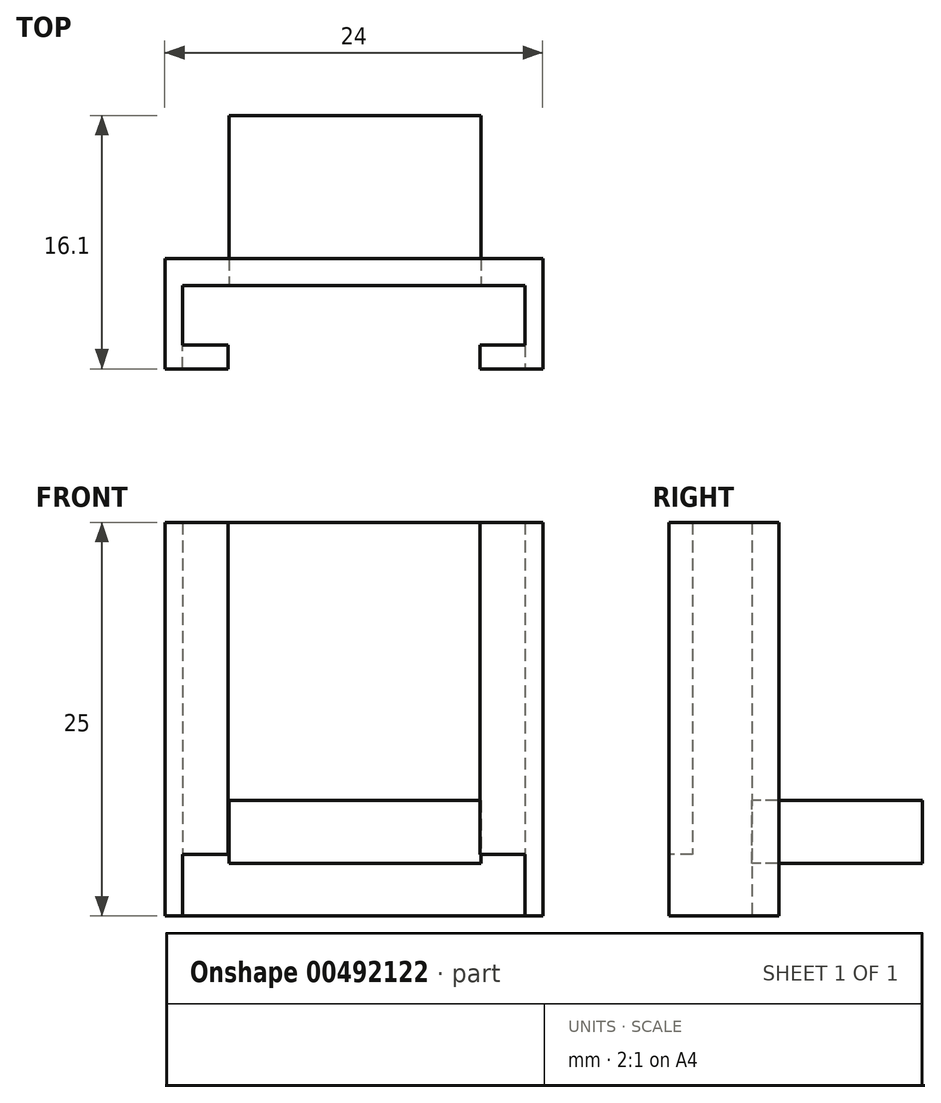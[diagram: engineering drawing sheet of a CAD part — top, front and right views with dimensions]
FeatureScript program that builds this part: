
annotation { "Feature Type Name" : "Feature", "Feature Type Description" : "" }
export const myFeature = defineFeature(function(context is Context, id is Id, definition is map)
    precondition{}
    {
        {
            var Q0;
            Q0=qCreatedBy(makeId("Top.planeOp"),FACE);
            var sketch = newSketch(context, id + "F0", { "sketchPlane" : qUnion([Q0])});
            skLineSegment(sketch, "E0", {"start": v(-20.1, 8.38) * mm, "end": v(-8.1, 8.38) * mm});
            skLineSegment(sketch, "E1", {"start": v(-8.1, 8.38) * mm, "end": v(-8.1, 1.38) * mm});
            skLineSegment(sketch, "E2", {"start": v(-8.1, 1.38) * mm, "end": v(-12.1, 1.38) * mm});
            skLineSegment(sketch, "E3", {"start": v(-12.1, 1.38) * mm, "end": v(-12.1, 2.88) * mm});
            skLineSegment(sketch, "E4", {"start": v(-12.1, 2.88) * mm, "end": v(-9.23, 2.88) * mm});
            skLineSegment(sketch, "E5", {"start": v(-9.23, 2.88) * mm, "end": v(-9.23, 6.68) * mm});
            skLineSegment(sketch, "E6", {"start": v(-9.23, 6.68) * mm, "end": v(-20.1, 6.68) * mm});
            skLineSegment(sketch, "E7", {"start": v(-20.1, 8.38) * mm, "end": v(-20.1, 6.68) * mm});
            skLineSegment(sketch, "E8.MirrorCS", {"start": v(-32.1, 8.38) * mm, "end": v(-32.1, 1.38) * mm});
            skLineSegment(sketch, "E9.MirrorCS", {"start": v(-20.1, 8.38) * mm, "end": v(-32.1, 8.38) * mm});
            skLineSegment(sketch, "E10.MirrorCS", {"start": v(-30.98, 6.68) * mm, "end": v(-20.1, 6.68) * mm});
            skLineSegment(sketch, "E11.MirrorCS", {"start": v(-28.1, 2.88) * mm, "end": v(-30.98, 2.88) * mm});
            skLineSegment(sketch, "E12.MirrorCS", {"start": v(-32.1, 1.38) * mm, "end": v(-28.1, 1.38) * mm});
            skLineSegment(sketch, "E13.MirrorCS", {"start": v(-30.98, 2.88) * mm, "end": v(-30.98, 6.68) * mm});
            skLineSegment(sketch, "E14.MirrorCS", {"start": v(-28.1, 1.38) * mm, "end": v(-28.1, 2.88) * mm});
            skSolve(sketch);
        }
        {
            var Q0;
            Q0=makeQuery(id+"F0.imprint","IMPRINT",FACE,{"disambiguationData":[TD([[makeQuery(id+"F0.imprint","IMPRINT",EDGE,{"derivedFrom":sQuery(id+"F0.wireOp",EDGE,"E0")}),-1.0]])]});
            var Q1;
            Q1=makeQuery(id+"F0.imprint","IMPRINT",FACE,{"disambiguationData":[TD([[makeQuery(id+"F0.imprint","IMPRINT",EDGE,{"derivedFrom":sQuery(id+"F0.wireOp",EDGE,"E7")}),-1.0]])]});
            extrude(context, id + "F1", {"entities" : qUnion([Q0, Q1]), "depth" : 25 * mm});
        }
        {
            var Q0;
            Q0=qCreatedBy(makeId("Front.planeOp"),FACE);
            var sketch = newSketch(context, id + "F2", { "sketchPlane" : qUnion([Q0])});
            skLineSegment(sketch, "E15", {"start": v(-30.99, 3.9) * mm, "end": v(-9.24, 3.9) * mm});
            skLineSegment(sketch, "E16", {"start": v(-9.24, 3.9) * mm, "end": v(-9.24, -0.1) * mm});
            skLineSegment(sketch, "E17", {"start": v(-9.24, -0.1) * mm, "end": v(-30.99, -0.1) * mm});
            skLineSegment(sketch, "E18", {"start": v(-30.99, -0.1) * mm, "end": v(-30.99, 3.9) * mm});
            skSolve(sketch);
        }
        {
            var Q0;
            Q0 = qSketchRegion(id + "F2", true);
            extrude(context, id + "F3", {"entities" : qUnion([Q0]), "operationType" : NewBodyOperationType.REMOVE, "oppositeDirection" : true, "depth" : 3.38 * mm});
        }
        {
            var Q0;
            Q0=makeQuery(id+"F1.opExtrude","SWEPT_FACE",FACE,{"disambiguationData":[OSD([sQuery(id+"F0.wireOp",EDGE,"E0"),sQuery(id+"F0.wireOp",EDGE,"E9.MirrorCS")])]});
            var sketch = newSketch(context, id + "F4", { "sketchPlane" : qUnion([Q0])});
            skLineSegment(sketch, "E19", {"start": v(12.03, 7.33) * mm, "end": v(28.03, 7.33) * mm});
            skLineSegment(sketch, "E20", {"start": v(12.03, 3.33) * mm, "end": v(28.03, 3.33) * mm});
            skLineSegment(sketch, "E21", {"start": v(12.03, 7.33) * mm, "end": v(12.03, 3.33) * mm});
            skLineSegment(sketch, "E22", {"start": v(28.03, 7.33) * mm, "end": v(28.03, 3.33) * mm});
            skSolve(sketch);
        }
        {
            var Q0;
            Q0=makeQuery(id+"F4.imprint","IMPRINT",FACE,{"disambiguationData":[TD([[makeQuery(id+"F4.imprint","IMPRINT",EDGE,{"derivedFrom":sQuery(id+"F4.wireOp",EDGE,"E19")}),-1.0]])]});
            extrude(context, id + "F5", {"entities" : qUnion([Q0]), "depth" : 9.1 * mm, "hasSecondDirection" : true, "secondDirectionBound" : SecondDirectionBoundingType.UP_TO_NEXT, "secondDirectionOppositeDirection" : true, "secondDirectionDepth" : 25 * mm});
        }
    });
